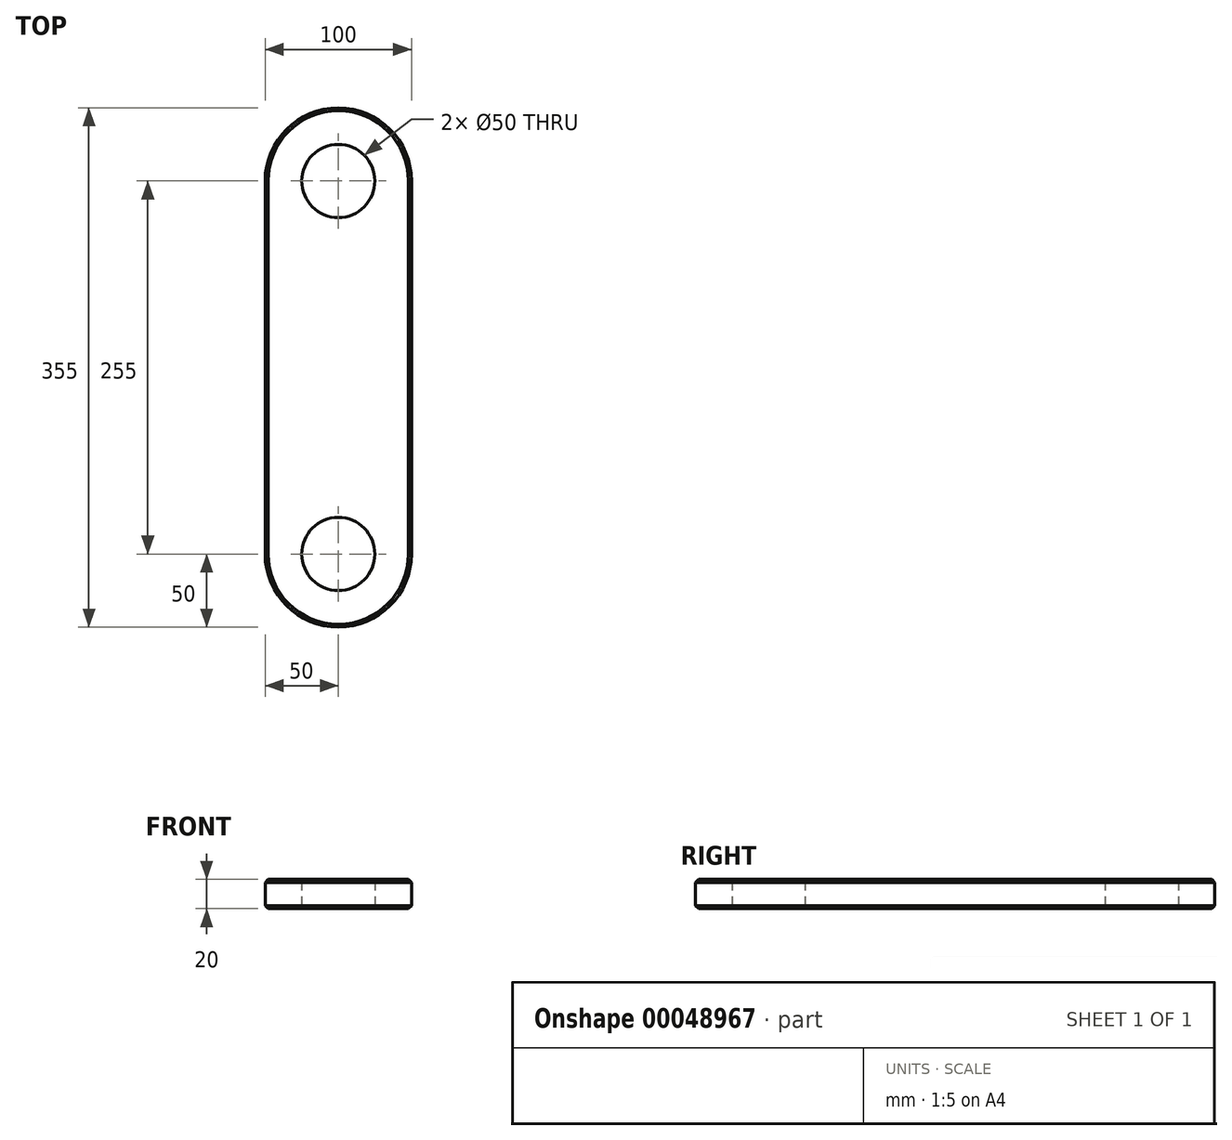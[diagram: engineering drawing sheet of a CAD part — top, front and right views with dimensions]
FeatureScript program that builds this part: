
annotation { "Feature Type Name" : "Feature", "Feature Type Description" : "" }
export const myFeature = defineFeature(function(context is Context, id is Id, definition is map)
    precondition{}
    {
        {
            var Q0;
            Q0=qCreatedBy(makeId("Top.planeOp"),FACE);
            var sketch = newSketch(context, id + "F0", { "sketchPlane" : qUnion([Q0])});
            skLineSegment(sketch, "E0.rect.bottom", {"start": v(50, 127.5) * mm, "end": v(-50, 127.5) * mm, "construction": true});
            skLineSegment(sketch, "E0.rect.top", {"start": v(50, -127.5) * mm, "end": v(-50, -127.5) * mm, "construction": true});
            skLineSegment(sketch, "E0.rect.left", {"start": v(50, 127.5) * mm, "end": v(50, -127.5) * mm});
            skLineSegment(sketch, "E0.rect.right", {"start": v(-50, 127.5) * mm, "end": v(-50, -127.5) * mm});
            skPoint(sketch, "E0.rect.middle", {"position": v(0, 0) * mm});
            skArc(sketch, "E1", {"start": v(-50, 127.5) * mm, "mid": v(0, 177.5) * mm, "end": v(50, 127.5) * mm});
            skArc(sketch, "E2", {"start": v(50, -127.5) * mm, "mid": v(0, -177.5) * mm, "end": v(-50, -127.5) * mm});
            skCircle(sketch, "E3", {"center": v(0, 127.5) * mm, "radius": 25 * mm});
            skCircle(sketch, "E4", {"center": v(0, -127.5) * mm, "radius": 25 * mm});
            skSolve(sketch);
        }
        {
            var Q0;
            Q0=makeQuery(id+"F0.imprint","IMPRINT",FACE,{"disambiguationData":[TD([[makeQuery(id+"F0.imprint","IMPRINT",EDGE,{"derivedFrom":sQuery(id+"F0.wireOp",EDGE,"E0.rect.left")}),-1.0]])]});
            extrude(context, id + "F1", {"entities" : qUnion([Q0]), "depth" : 20 * mm});
        }
        {
            var Q0;
            Q0=makeQuery(id+"F1.opExtrude","CAP_EDGE",EDGE,{"disambiguationData":[OSD([sQuery(id+"F0.wireOp",EDGE,"E0.rect.left")])],"isStart":false});
            var Q1;
            Q1=makeQuery(id+"F1.opExtrude","CAP_EDGE",EDGE,{"disambiguationData":[OSD([sQuery(id+"F0.wireOp",EDGE,"E2")])],"isStart":false});
            var Q2;
            Q2=makeQuery(id+"F1.opExtrude","CAP_EDGE",EDGE,{"disambiguationData":[OSD([sQuery(id+"F0.wireOp",EDGE,"E0.rect.right")])],"isStart":false});
            var Q3;
            Q3=makeQuery(id+"F1.opExtrude","CAP_EDGE",EDGE,{"disambiguationData":[OSD([sQuery(id+"F0.wireOp",EDGE,"E1")])],"isStart":false});
            var Q4;
            Q4=makeQuery(id+"F1.opExtrude","CAP_EDGE",EDGE,{"disambiguationData":[OSD([sQuery(id+"F0.wireOp",EDGE,"E0.rect.left")])],"isStart":true});
            var Q5;
            Q5=makeQuery(id+"F1.opExtrude","CAP_EDGE",EDGE,{"disambiguationData":[OSD([sQuery(id+"F0.wireOp",EDGE,"E2")])],"isStart":true});
            var Q6;
            Q6=makeQuery(id+"F1.opExtrude","CAP_EDGE",EDGE,{"disambiguationData":[OSD([sQuery(id+"F0.wireOp",EDGE,"E1")])],"isStart":true});
            var Q7;
            Q7=makeQuery(id+"F1.opExtrude","CAP_EDGE",EDGE,{"disambiguationData":[OSD([sQuery(id+"F0.wireOp",EDGE,"E0.rect.right")])],"isStart":true});
            chamfer(context, id + "F2", {"entities" : qUnion([Q0, Q1, Q2, Q3, Q4, Q5, Q6, Q7]), "chamferType" : ChamferType.OFFSET_ANGLE, "width" : 2 * mm, "oppositeDirection" : false, "angle" : 45 * degree, "tangentPropagation" : true});
        }
    });
